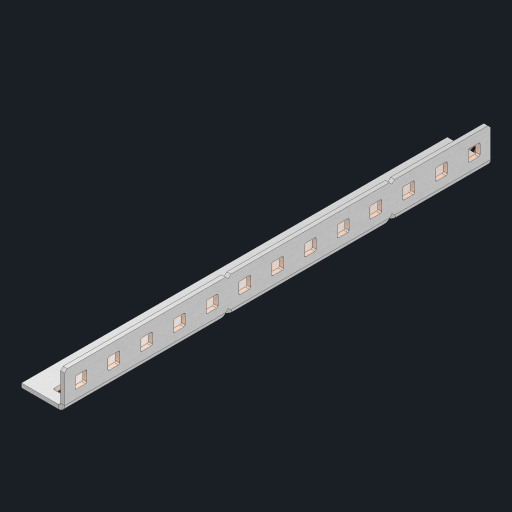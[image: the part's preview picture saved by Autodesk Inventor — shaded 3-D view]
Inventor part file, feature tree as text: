
AUTODESK INVENTOR PART (.ipt)
format: ipt  version: 2023 (Build 270158000, 158)  size: 640,000 bytes
history: native  units: in
note: dims shown in document units (in); Inventor stores cm internally (conversion verified against a paired STEP export)
features: other x31, extrude x25, sheet_metal_op x10, sketch x8, mirror x1, pattern_linear x1, chamfer x1
ambient origin geometry x8: Origin, YZ Plane, XZ Plane, XY Plane, X Axis, Y Axis, Z Axis, Center Point
bodies: Solid1 (feature_tree), Body (feature_tree)
feature tree (77):
  other  "Flange Pattern Plane"
  sheet_metal_op  "Flange Pattern"
  sheet_metal_op  "Body Pattern"
  other  "Arc Length"
  mirror  "Notch Mirror"
  pattern_linear  "Notch Pattern"  Spacing1=0.25in  [1 undecoded]
  chamfer  "End Chamfer"
  extrude  "Half Cut"  Depth=0.0625in
  sketch  "Sketch1"  dims[d0=1.5in]
  other  "Plate1"
  sketch  "Sketch2"  dims[d1=6.5in]
  other  "Plate2"
  sheet_metal_op  "Bend1"
  sheet_metal_op  "Corner1"
  sketch  "Sketch3"  dims[d2=0.0625in]
  other  "Flange Pattern Sketch"
  sketch  "Sketch7"  dims[d3=0.0625in]
  other  "Srf1"
  other  "Srf2"
  sketch  "Sketch8"  dims[d4=0.0312in]
  sketch  "Sketch9"  dims[d5=0.125in]
  other  "Srf91"
  sheet_metal_op  "Body Pattern Sketch"
  other  "Srf92"
  sketch  "Sketch13"  dims[d6=0.0625in]
  sketch  "Sketch14"  dims[d7=0.5in d8=90.0deg d9=0.0312in d10=0.25in d11=0.0625in d12=0.0625in d16=0.182in d17=0.02in d18=0.0625in d19=0.0in d20=0.25in d21=0.25in d46=0.172in d47=1.0in d48=0.0in d49=0.182in d50=0.02in d51=0.25in d52=0.25in d53=0.0625in d54=0.0in d55=0.172in d56=1.0in d57=0.0in d60=5.1181in d62=0.5in d63=0.3937in d65=0.5in d85=0.1473in d86=0.1782in d88=0.04in d89=0.0625in d90=0.0in d91=0.04in d92=0.0491in d95=2.5in d96=0.04in d97=0.25in d98=45.0deg d101=0.0in d102=2.497in d131=0.5in d132=5.1181in d134=0.5in d139=0.5in]
  other  "Srf856"
  other  "Srf1310"
  other  "Srf1311"
  other  "Srf1312"
  other  "Srf1376"
  other  "Srf1377"
  other  "Srf1728"
  other  "Srf1755"
  other  "Srf1878"
  other  "Srf1879"
  other  "Srf1880"
  other  "Srf1881"
  other  "Srf1882"
  other  "Srf1883"
  other  "Srf1884"
  other  "Srf1942"
  other  "Srf1943"
  other  "Srf1944"
  other  "Srf1945"
  other  "Srf1946"
  other  "Srf1947"
  other  "Srf1948"
  sheet_metal_op  "Flange Stamp"
  sheet_metal_op  "Flange Circle"
  sheet_metal_op  "Body Stamp"
  sheet_metal_op  "Body Circle"
  sheet_metal_op  "Notch"
  extrude  "ExtrusionSrf2"  Depth=0.0625in
  extrude  "ExtrusionSrf92"  Depth=0.5in
  extrude  "ExtrusionSrf856"  Depth=0.02in
  extrude  "ExtrusionSrf1310"  Depth=0.0625in
  extrude  "ExtrusionSrf1311"  TaperAngle=0.0deg  [1 undecoded]
  extrude  "ExtrusionSrf1312"  Depth=0.5in
  extrude  "ExtrusionSrf1376"  Depth=0.5in
  extrude  "ExtrusionSrf1377"  Depth=0.5in
  extrude  "ExtrusionSrf1728"  Depth=0.5in TaperAngle=0.0deg
  extrude  "ExtrusionSrf1755"  Depth=0.5in
  extrude  "ExtrusionSrf1878"  Depth=0.02in
  extrude  "ExtrusionSrf1879"  Depth=0.5in
  extrude  "ExtrusionSrf1880"  Depth=0.5in
  extrude  "ExtrusionSrf1881"  Depth=0.0625in
  extrude  "ExtrusionSrf1882"  TaperAngle=0.0deg  [1 undecoded]
  extrude  "ExtrusionSrf1883"  Depth=0.5in
  extrude  "ExtrusionSrf1884"  Depth=0.5in TaperAngle=0.0deg
  extrude  "ExtrusionSrf1942"  Depth=0.5in
  extrude  "ExtrusionSrf1943"  Depth=0.5in
  extrude  "ExtrusionSrf1944"  Depth=0.5in
  extrude  "ExtrusionSrf1945"  Depth=0.5in
  extrude  "ExtrusionSrf1946"  Depth=0.5in
  extrude  "ExtrusionSrf1947"  Depth=0.0625in
  extrude  "ExtrusionSrf1948"  TaperAngle=0.0deg  [1 undecoded]
note: 4 required parameter values undecoded (feature->parameter linkage not recoverable at this tier; creation-order binding heuristic only, values carry confidence <= 0.55)
